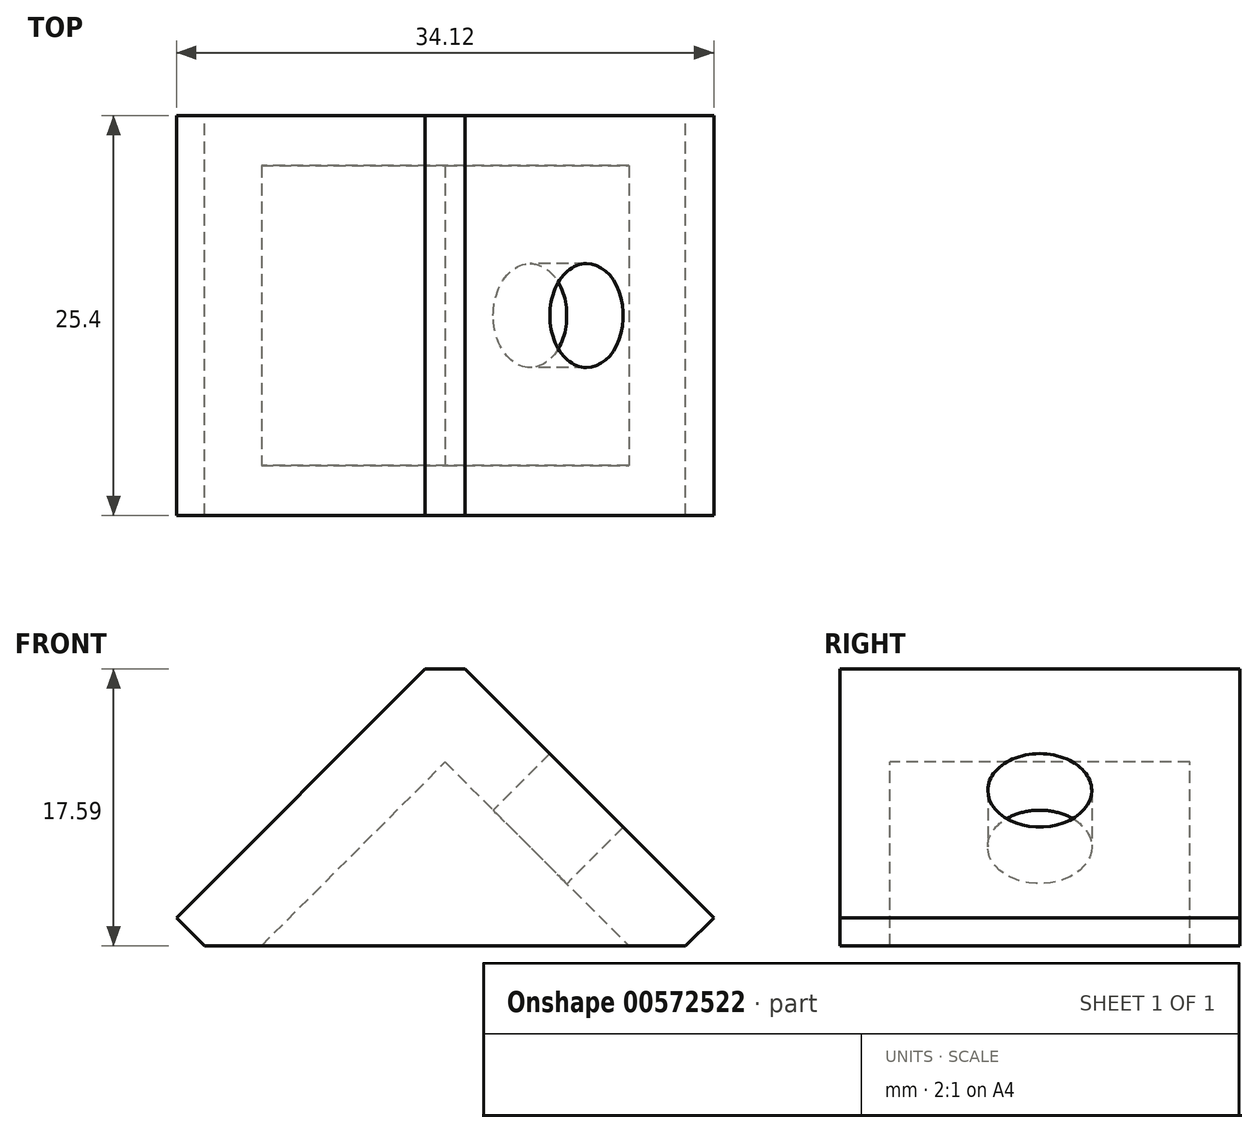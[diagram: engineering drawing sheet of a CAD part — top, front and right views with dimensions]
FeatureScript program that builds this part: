
annotation { "Feature Type Name" : "Feature", "Feature Type Description" : "" }
export const myFeature = defineFeature(function(context is Context, id is Id, definition is map)
    precondition{}
    {
        {
            var Q0;
            Q0=qCreatedBy(makeId("Front.planeOp"),FACE);
            var sketch = newSketch(context, id + "F0", { "sketchPlane" : qUnion([Q0])});
            skLineSegment(sketch, "E0", {"start": v(-15.27, 0) * mm, "end": v(15.27, 0) * mm});
            skLineSegment(sketch, "E1", {"start": v(15.27, 0) * mm, "end": v(17.06, 1.8) * mm});
            skLineSegment(sketch, "E2", {"start": v(17.06, 1.8) * mm, "end": v(1.27, 17.59) * mm});
            skLineSegment(sketch, "E3", {"start": v(1.27, 17.59) * mm, "end": v(-1.27, 17.59) * mm});
            skLineSegment(sketch, "E4", {"start": v(-17.06, 1.8) * mm, "end": v(-1.27, 17.59) * mm});
            skLineSegment(sketch, "E5", {"start": v(-17.06, 1.8) * mm, "end": v(-15.27, 0) * mm});
            skLineSegment(sketch, "E6", {"start": v(0, 17.59) * mm, "end": v(0, 0) * mm, "construction": true});
            skLineSegment(sketch, "E7", {"start": v(-11.67, 0) * mm, "end": v(0, 11.67) * mm, "construction": true});
            skLineSegment(sketch, "E8", {"start": v(0, 11.67) * mm, "end": v(11.67, 0) * mm, "construction": true});
            skSolve(sketch);
        }
        {
            var Q0;
            Q0=makeQuery(id+"F0.imprint","IMPRINT",FACE,{"disambiguationData":[TD([[makeQuery(id+"F0.imprint","IMPRINT",EDGE,{"derivedFrom":sQuery(id+"F0.wireOp",EDGE,"E0")}),1.0]])]});
            extrude(context, id + "F1", {"entities" : qUnion([Q0]), "endBound" : BoundingType.SYMMETRIC, "depth" : 25.4 * mm, "offsetDistance" : 25.4 * mm});
        }
        {
            var Q0;
            Q0=qCreatedBy(makeId("Front.planeOp"),FACE);
            var sketch = newSketch(context, id + "F2", { "sketchPlane" : qUnion([Q0])});
            skLineSegment(sketch, "E9", {"start": v(-11.67, 0) * mm, "end": v(0, 11.67) * mm});
            skLineSegment(sketch, "E10", {"start": v(0, 11.67) * mm, "end": v(11.67, 0) * mm});
            skLineSegment(sketch, "E11", {"start": v(11.67, 0) * mm, "end": v(-11.67, 0) * mm});
            skSolve(sketch);
        }
        {
            var Q0;
            Q0 = qSketchRegion(id + "F2", true);
            extrude(context, id + "F3", {"entities" : qUnion([Q0]), "operationType" : NewBodyOperationType.REMOVE, "endBound" : BoundingType.SYMMETRIC, "oppositeDirection" : true, "depth" : 19.05 * mm, "offsetDistance" : 25.4 * mm});
        }
        {
            var Q0;
            Q0=makeQuery(id+"F3.boolean.opBoolean","COPY",FACE,{"derivedFrom":makeQuery(id+"F3.opExtrude","SWEPT_FACE",FACE,{"disambiguationData":[OSD([sQuery(id+"F2.wireOp",EDGE,"E10")])]})});
            var sketch = newSketch(context, id + "F4", { "sketchPlane" : qUnion([Q0])});
            skPoint(sketch, "E12", {"position": v(0, 0.63) * mm});
            skSolve(sketch);
        }
        {
            var Q0;
            Q0=sQuery(id+"F4.wireOp",VERTEX,"E12");
            var Q1;
            Q1=makeQuery(id+"F1.opExtrude","SWEPT_BODY",BODY,{"disambiguationData":[OSD([sQuery(id+"F0.wireOp",EDGE,"E0"),sQuery(id+"F0.wireOp",EDGE,"E1"),sQuery(id+"F0.wireOp",EDGE,"E2"),sQuery(id+"F0.wireOp",EDGE,"E3"),sQuery(id+"F0.wireOp",EDGE,"E4"),sQuery(id+"F0.wireOp",EDGE,"E5")])]});
            hole(context, id + "F5", {"style" : HoleStyle.SIMPLE, "endStyle" : HoleEndStyle.THROUGH, "holeDiameter" : 6.6 * mm, "tappedDepth" : 12.7 * mm, "tapClearance" : 3, "startFromSketch" : true, "locations" : qUnion([Q0]), "scope" : qUnion([Q1])});
        }
    });
